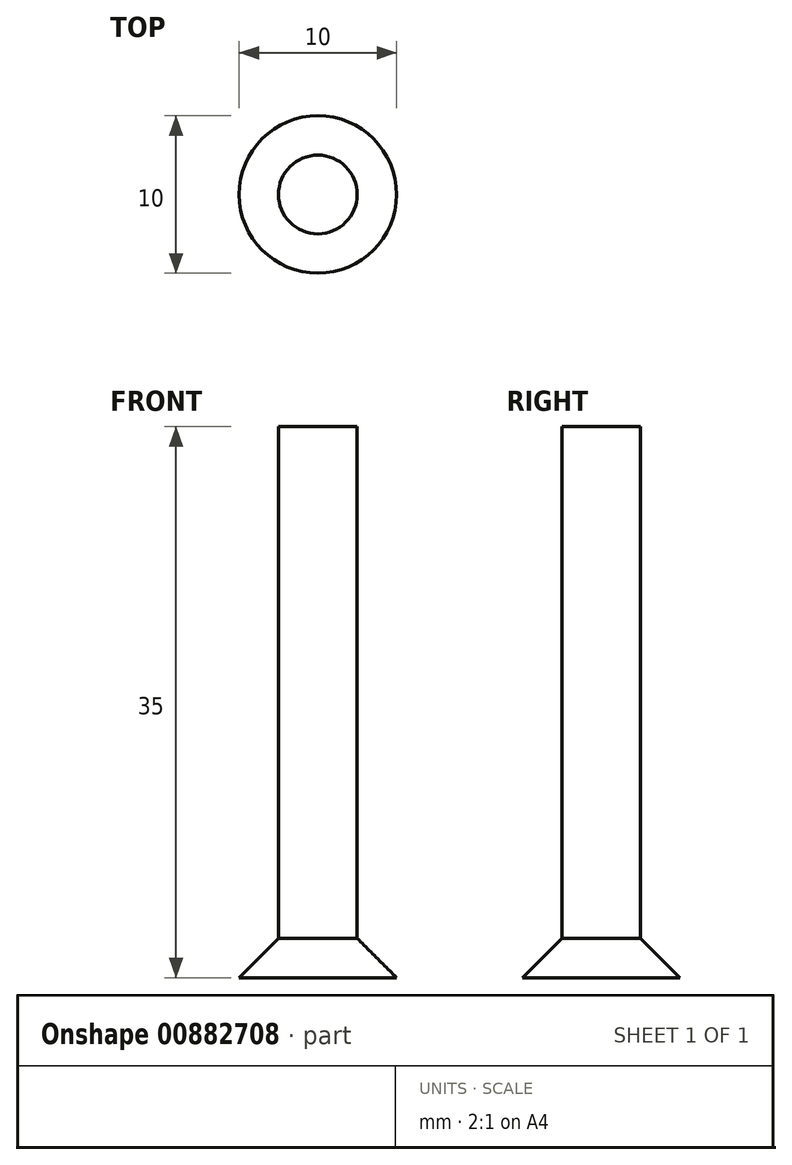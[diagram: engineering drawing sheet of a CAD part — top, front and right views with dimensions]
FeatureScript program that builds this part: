
annotation { "Feature Type Name" : "Feature", "Feature Type Description" : "" }
export const myFeature = defineFeature(function(context is Context, id is Id, definition is map)
    precondition{}
    {
        {
            var Q0;
            Q0=qCreatedBy(makeId("Top.planeOp"),FACE);
            var sketch = newSketch(context, id + "F0", { "sketchPlane" : qUnion([Q0])});
            skCircle(sketch, "E0", {"center": v(0, 0) * mm, "radius": 5 * mm});
            skPoint(sketch, "E1", {"position": v(5, 0) * mm});
            skSolve(sketch);
        }
        {
            var Q0;
            Q0=qSketchRegion(id+"F0",true);
            extrude(context, id + "F1", {"entities" : qUnion([Q0]), "depth" : 2.5 * mm, "offsetDistance" : 25 * mm});
        }
        {
            var Q0;
            Q0=makeQuery(id+"F1.opExtrude","CAP_EDGE",EDGE,{"disambiguationData":[OSD([sQuery(id+"F0.wireOp",EDGE,"E0")])],"isStart":false});
            chamfer(context, id + "F2", {"entities" : qUnion([Q0]), "width" : 2.5 * mm, "tangentPropagation" : true});
        }
        {
            var Q0;
            Q0=makeQuery(id+"F1.opExtrude","CAP_FACE",FACE,{"disambiguationData":[OSD([sQuery(id+"F0.wireOp",EDGE,"E0")])],"isStart":false});
            extrude(context, id + "F3", {"entities" : qUnion([Q0]), "operationType" : NewBodyOperationType.ADD, "depth" : 32.5 * mm, "offsetDistance" : 25 * mm});
        }
    });
